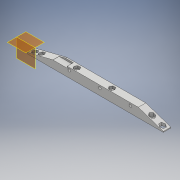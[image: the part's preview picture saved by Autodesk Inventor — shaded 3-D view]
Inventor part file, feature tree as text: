
AUTODESK INVENTOR PART (.ipt)
format: ipt  version: 2018.2 (Build 222227000, 227)  size: 266,752 bytes
history: native  units: mm
features: extrude x11, sketch x10, plane x7
ambient origin geometry x8: Origin, YZ Plane, XZ Plane, XY Plane, X Axis, Y Axis, Z Axis, Center Point
bodies: Solid1 (feature_tree)
feature tree (28):
  sketch  "Sketch1"  dims[d1=9.0mm d2=90.0deg]
  plane  "Work Plane2"
  sketch  "Sketch2"  dims[d4=3.2mm d6=3.2mm]
  plane  "Work Plane1"
  extrude  "klocek"  TaperAngle=90.0deg  [1 undecoded]
  plane  "Work Plane3"
  extrude  "prowadzenie osi"  Depth=3.2mm
  plane  "Work Plane4"
  sketch  "Sketch7"  dims[d9=60.5mm d13=3.2mm]
  sketch  "Sketch8"  dims[d15=3.2mm d17=3.2mm]
  extrude  "przedni skos"  Depth=42.0mm
  extrude  "tylni skos"  Depth=3.2mm
  plane  "Work Plane7"
  sketch  "Sketch5"  dims[d7=3.2mm d8=42.0mm]
  extrude  "hex insert middle"  Depth=3.2mm
  plane  "Work Plane6"
  sketch  "Sketch9"  dims[d18=36.5mm d26=3.2mm]
  extrude  "hex insert rear 1"  Depth=3.2mm
  plane  "Work Plane5"
  extrude  "hex insert rear 2"  Depth=3.2mm
  extrude  "hex insert front 1"  Depth=15.0mm
  extrude  "hex insert front 2"  Depth=11.0mm
  extrude  "ciecie przod"  Depth=5.9mm
  extrude  "sensor linii"  Depth=8.0mm
  sketch  "Sketch10"  dims[d27=48.0mm d28=3.2mm]
  sketch  "Sketch16"  dims[d29=42.0mm d32=15.0mm]
  sketch  "Sketch17"  dims[d33=5.0mm d38=11.0mm]
  sketch  "Sketch18"  dims[d39=0.0mm d61=3.2mm d62=8.0mm d63=12.5mm d64=52.0mm d65=36.5mm d67=11.0mm d68=0.0mm d70=7.5mm d71=0.0mm d77=5.0mm d78=0.0mm d80=10.0mm d81=30.0mm d82=3.0mm d83=0.0mm d84=8.5mm d85=0.0mm d86=10.0mm d87=40.0mm d88=7.0mm d89=0.0mm d91=9.0mm d92=0.0mm d93=5.9mm d94=9.0mm d95=0.0mm d96=10.0mm d97=0.0mm d98=5.9mm d99=5.9mm d100=5.9mm d102=2.0mm d103=17.0mm d104=2.5mm d105=7.3mm d106=0.0mm d108=4.0mm d109=4.0mm d110=4.0mm d111=4.0mm d112=4.0mm d113=4.0mm d114=8.0mm d115=73.0mm d118=5.9mm d122=2.0mm d123=5.9mm]
note: 1 required parameter value undecoded (feature->parameter linkage not recoverable at this tier; creation-order binding heuristic only, values carry confidence <= 0.55)
